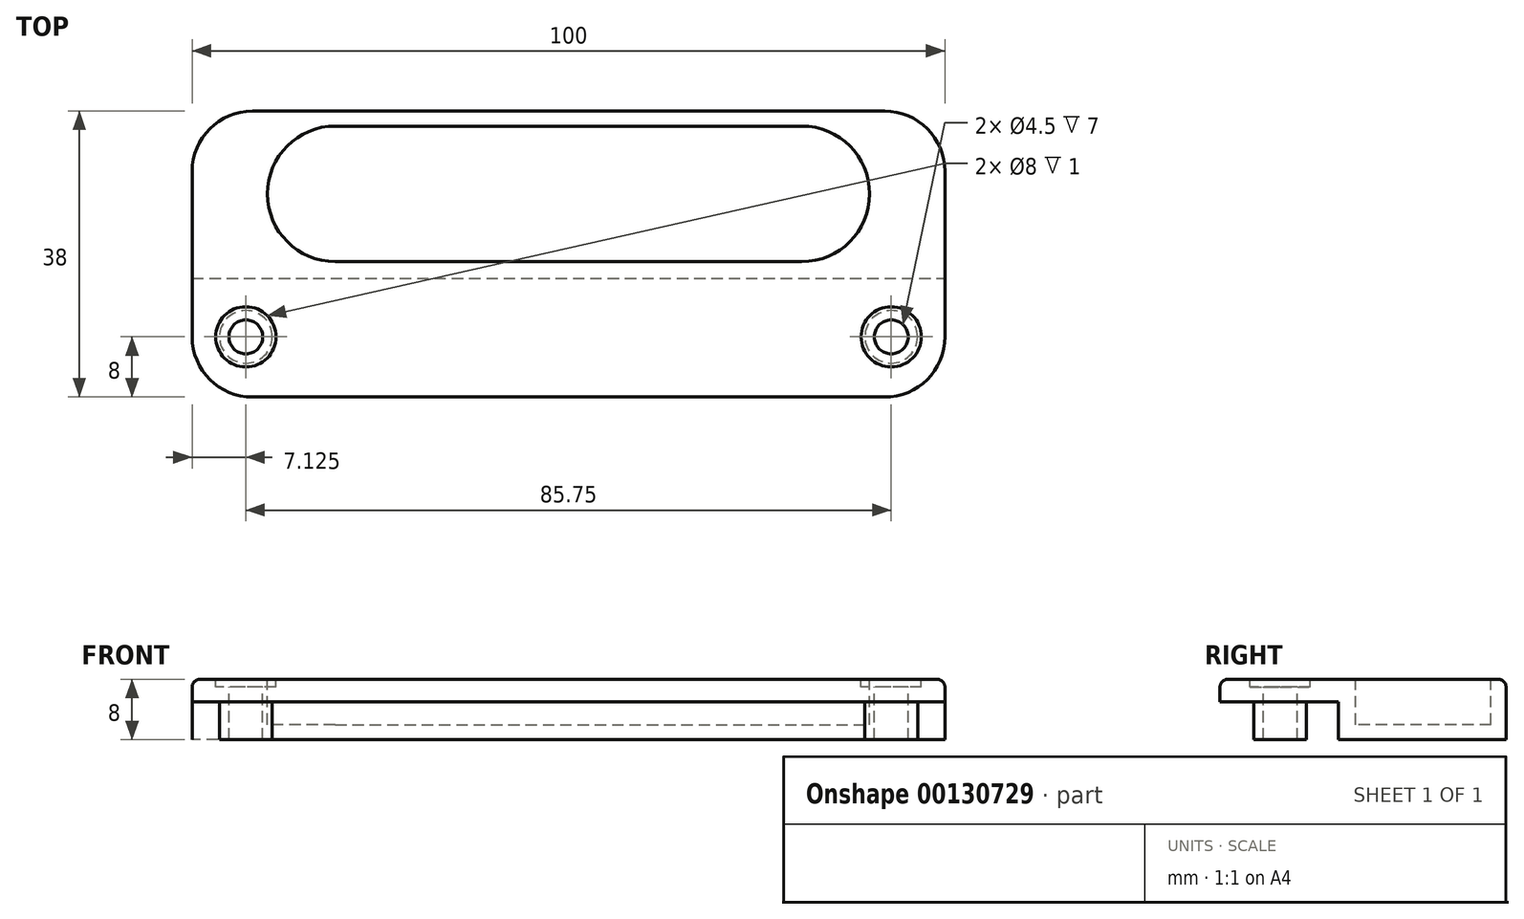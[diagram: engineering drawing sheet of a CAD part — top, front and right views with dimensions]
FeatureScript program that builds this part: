
annotation { "Feature Type Name" : "Feature", "Feature Type Description" : "" }
export const myFeature = defineFeature(function(context is Context, id is Id, definition is map)
    precondition{}
    {
        {
            var Q0;
            Q0=qCreatedBy(makeId("Top.planeOp"),FACE);
            var sketch = newSketch(context, id + "F0", { "sketchPlane" : qUnion([Q0])});
            skLineSegment(sketch, "E0.bottom", {"start": v(42, -19) * mm, "end": v(-42, -19) * mm});
            skLineSegment(sketch, "E0.top", {"start": v(42, 19) * mm, "end": v(-42, 19) * mm});
            skLineSegment(sketch, "E0.left", {"start": v(50, -11) * mm, "end": v(50, 11) * mm});
            skLineSegment(sketch, "E0.right", {"start": v(-50, -11) * mm, "end": v(-50, 11) * mm});
            skPoint(sketch, "E0.middle", {"position": v(0, 0) * mm});
            skPoint(sketch, "E1.visualSharp", {"position": v(-50, 19) * mm});
            skArc(sketch, "E1.filletArc", {"start": v(-42, 19) * mm, "mid": v(-47.66, 16.66) * mm, "end": v(-50, 11) * mm});
            skPoint(sketch, "E2.visualSharp", {"position": v(50, 19) * mm});
            skArc(sketch, "E2.filletArc", {"start": v(50, 11) * mm, "mid": v(47.66, 16.66) * mm, "end": v(42, 19) * mm});
            skPoint(sketch, "E3.visualSharp", {"position": v(50, -19) * mm});
            skArc(sketch, "E3.filletArc", {"start": v(42, -19) * mm, "mid": v(47.66, -16.66) * mm, "end": v(50, -11) * mm});
            skPoint(sketch, "E4.visualSharp", {"position": v(-50, -19) * mm});
            skArc(sketch, "E4.filletArc", {"start": v(-50, -11) * mm, "mid": v(-47.66, -16.66) * mm, "end": v(-42, -19) * mm});
            skLineSegment(sketch, "E5.bottom", {"start": v(-31, 17) * mm, "end": v(31, 17) * mm});
            skLineSegment(sketch, "E5.top", {"start": v(-31, -1) * mm, "end": v(31, -1) * mm});
            skLineSegment(sketch, "E5.left", {"start": v(-40, 8) * mm, "end": v(-40, 8) * mm});
            skLineSegment(sketch, "E5.right", {"start": v(40, 8) * mm, "end": v(40, 8) * mm});
            skPoint(sketch, "E6.visualSharp", {"position": v(-40, 17) * mm});
            skArc(sketch, "E6.filletArc", {"start": v(-31, 17) * mm, "mid": v(-37.36, 14.36) * mm, "end": v(-40, 8) * mm});
            skPoint(sketch, "E7.visualSharp", {"position": v(-40, -1) * mm});
            skArc(sketch, "E7.filletArc", {"start": v(-40, 8) * mm, "mid": v(-37.36, 1.64) * mm, "end": v(-31, -1) * mm});
            skPoint(sketch, "E8.visualSharp", {"position": v(40, -1) * mm});
            skArc(sketch, "E8.filletArc", {"start": v(31, -1) * mm, "mid": v(37.36, 1.64) * mm, "end": v(40, 8) * mm});
            skPoint(sketch, "E9.visualSharp", {"position": v(40, 17) * mm});
            skArc(sketch, "E9.filletArc", {"start": v(40, 8) * mm, "mid": v(37.36, 14.36) * mm, "end": v(31, 17) * mm});
            skPoint(sketch, "E10", {"position": v(-42.88, -11) * mm});
            skPoint(sketch, "E11.MirrorP", {"position": v(42.88, -11) * mm});
            skSolve(sketch);
        }
        {
            var Q0;
            Q0=makeQuery(id+"F0.imprint","IMPRINT",FACE,{"disambiguationData":[TD([[makeQuery(id+"F0.imprint","IMPRINT",EDGE,{"derivedFrom":sQuery(id+"F0.wireOp",EDGE,"E0.bottom")}),-1.0]])]});
            var Q1;
            Q1=makeQuery(id+"F0.imprint","IMPRINT",FACE,{"disambiguationData":[TD([[makeQuery(id+"F0.imprint","IMPRINT",EDGE,{"derivedFrom":sQuery(id+"F0.wireOp",EDGE,"E5.bottom")}),-1.0]])]});
            extrude(context, id + "F1", {"entities" : qUnion([Q0, Q1]), "oppositeDirection" : true, "depth" : 8 * mm});
        }
        {
            var Q0;
            Q0=makeQuery(id+"F0.imprint","IMPRINT",FACE,{"disambiguationData":[TD([[makeQuery(id+"F0.imprint","IMPRINT",EDGE,{"derivedFrom":sQuery(id+"F0.wireOp",EDGE,"E5.bottom")}),-1.0]])]});
            extrude(context, id + "F2", {"entities" : qUnion([Q0]), "operationType" : NewBodyOperationType.REMOVE, "oppositeDirection" : true, "depth" : 6 * mm});
        }
        {
            var Q0;
            Q0=sQuery(id+"F0.wireOp",VERTEX,"E10");
            var Q1;
            Q1=sQuery(id+"F0.wireOp",VERTEX,"E11.MirrorP");
            var Q2;
            Q2=makeQuery(id+"F1.opExtrude","SWEPT_BODY",BODY,{"disambiguationData":[OSD([sQuery(id+"F0.wireOp",EDGE,"E0.bottom"),sQuery(id+"F0.wireOp",EDGE,"E0.top"),sQuery(id+"F0.wireOp",EDGE,"E0.left"),sQuery(id+"F0.wireOp",EDGE,"E0.right"),sQuery(id+"F0.wireOp",EDGE,"E1.filletArc"),sQuery(id+"F0.wireOp",EDGE,"E2.filletArc"),sQuery(id+"F0.wireOp",EDGE,"E3.filletArc"),sQuery(id+"F0.wireOp",EDGE,"E4.filletArc")])]});
            hole(context, id + "F3", {"style" : HoleStyle.C_BORE, "endStyle" : HoleEndStyle.BLIND, "holeDiameter" : 4.5 * mm, "cBoreDiameter" : 8 * mm, "cBoreDepth" : 1 * mm, "holeDepth" : 12 * mm, "startFromSketch" : true, "locations" : qUnion([Q0, Q1]), "scope" : qUnion([Q2])});
        }
        {
            var Q0;
            Q0=makeQuery(id+"F1.opExtrude","CAP_FACE",FACE,{"disambiguationData":[OSD([sQuery(id+"F0.wireOp",EDGE,"E0.bottom"),sQuery(id+"F0.wireOp",EDGE,"E0.top"),sQuery(id+"F0.wireOp",EDGE,"E0.left"),sQuery(id+"F0.wireOp",EDGE,"E0.right"),sQuery(id+"F0.wireOp",EDGE,"E1.filletArc"),sQuery(id+"F0.wireOp",EDGE,"E2.filletArc"),sQuery(id+"F0.wireOp",EDGE,"E3.filletArc"),sQuery(id+"F0.wireOp",EDGE,"E4.filletArc")])],"isStart":false});
            var sketch = newSketch(context, id + "F4", { "sketchPlane" : qUnion([Q0])});
            skLineSegment(sketch, "E12", {"start": v(-50, 3.25) * mm, "end": v(50, 3.25) * mm});
            skSolve(sketch);
        }
        {
            var Q0;
            {var subQ8=sQuery(id+"F4.wireOp",EDGE,"E12");Q0=makeQuery(id+"F4.imprint","IMPRINT",FACE,{"disambiguationData":[TD([[makeQuery(id+"F4.imprint","IMPRINT",EDGE,{"derivedFrom":subQ8}),1.0]])]});}
            extrude(context, id + "F5", {"entities" : qUnion([Q0]), "operationType" : NewBodyOperationType.REMOVE, "oppositeDirection" : true, "depth" : 5 * mm});
        }
        {
            var Q0;
            Q0=makeQuery(id+"F5.boolean.opBoolean","COPY",FACE,{"derivedFrom":makeQuery(id+"F5.opExtrude","CAP_FACE",FACE,{"disambiguationData":[OSD([sQuery(id+"F0.wireOp",EDGE,"E0.bottom"),sQuery(id+"F0.wireOp",EDGE,"E0.top"),sQuery(id+"F0.wireOp",EDGE,"E0.left"),sQuery(id+"F0.wireOp",EDGE,"E0.right"),sQuery(id+"F0.wireOp",EDGE,"E1.filletArc"),sQuery(id+"F0.wireOp",EDGE,"E2.filletArc"),sQuery(id+"F0.wireOp",EDGE,"E3.filletArc"),sQuery(id+"F0.wireOp",EDGE,"E4.filletArc"),sQuery(id+"F3.hole-0.sketch.wireOp",EDGE,"core_line_2"),sQuery(id+"F3.hole-1.sketch.wireOp",EDGE,"core_line_2"),sQuery(id+"F4.wireOp",EDGE,"E12")])],"isStart":false})});
            var sketch = newSketch(context, id + "F6", { "sketchPlane" : qUnion([Q0])});
            skPoint(sketch, "E13.0", {"position": v(-42.88, 11) * mm});
            skPoint(sketch, "E13.1", {"position": v(42.88, 11) * mm});
            skCircle(sketch, "E14", {"center": v(-42.88, 11) * mm, "radius": 3.5 * mm});
            skCircle(sketch, "E15", {"center": v(42.88, 11) * mm, "radius": 3.5 * mm});
            skSolve(sketch);
        }
        {
            var Q0;
            Q0=makeQuery(id+"F6.imprint","IMPRINT",FACE,{"disambiguationData":[TD([[makeQuery(id+"F6.imprint","IMPRINT",EDGE,{"derivedFrom":sQuery(id+"F6.wireOp",EDGE,"E14")}),1.0]])]});
            var Q1;
            Q1=makeQuery(id+"F6.imprint","IMPRINT",FACE,{"disambiguationData":[TD([[makeQuery(id+"F6.imprint","IMPRINT",EDGE,{"derivedFrom":sQuery(id+"F6.wireOp",EDGE,"E15")}),1.0]])]});
            extrude(context, id + "F7", {"entities" : qUnion([Q0, Q1]), "operationType" : NewBodyOperationType.ADD, "depth" : 5 * mm});
        }
        {
            var Q0;
            Q0=makeQuery(id+"F1.opExtrude","CAP_EDGE",EDGE,{"disambiguationData":[OSD([sQuery(id+"F0.wireOp",EDGE,"E0.bottom")])],"isStart":true});
            var Q1;
            Q1=makeQuery(id+"F2.boolean.opBoolean","COPY",EDGE,{"derivedFrom":makeQuery(id+"F2.opExtrude","CAP_EDGE",EDGE,{"disambiguationData":[OSD([sQuery(id+"F0.wireOp",EDGE,"E5.top")])],"isStart":true})});
            fillet(context, id + "F8", {"entities" : qUnion([Q0, Q1]), "radius" : 1 * mm, "tangentPropagation" : true, "allowEdgeOverflow" : false});
        }
    });
